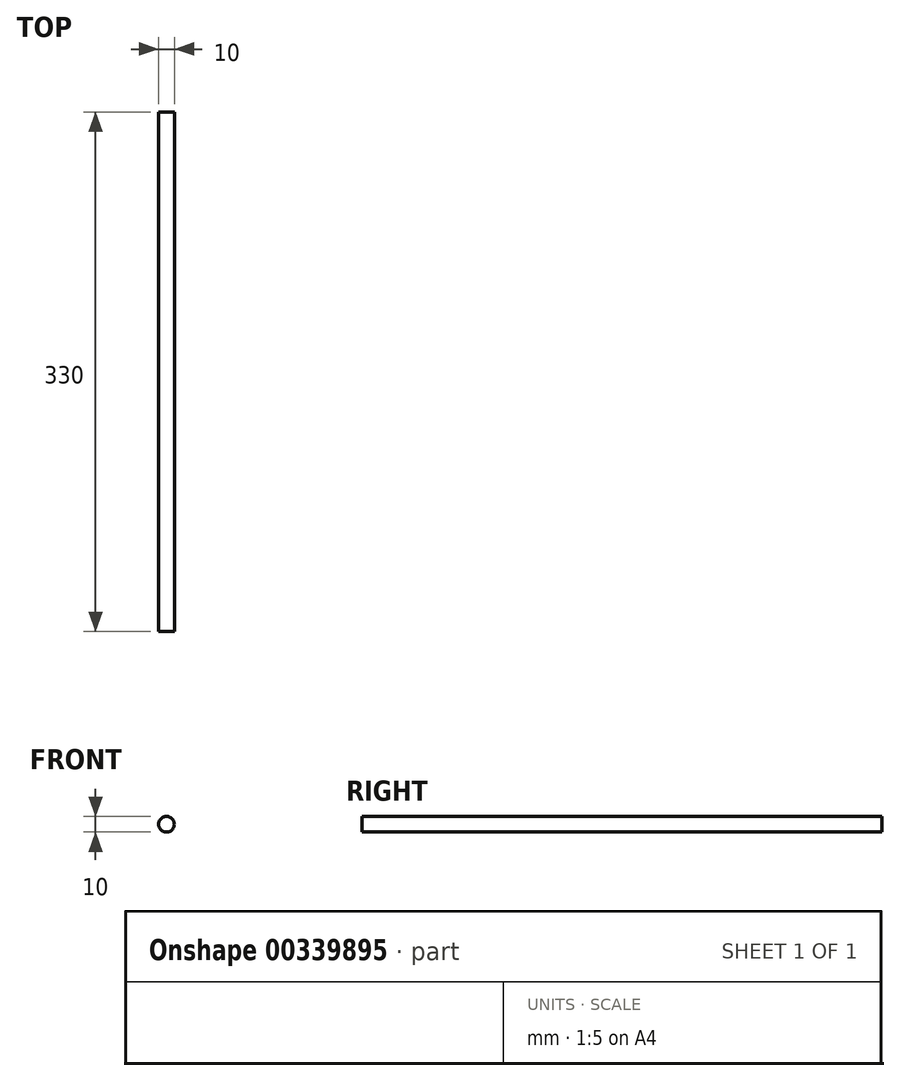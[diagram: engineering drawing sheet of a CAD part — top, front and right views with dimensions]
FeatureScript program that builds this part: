
annotation { "Feature Type Name" : "Feature", "Feature Type Description" : "" }
export const myFeature = defineFeature(function(context is Context, id is Id, definition is map)
    precondition{}
    {
        {
            var Q0;
            Q0=qCreatedBy(makeId("Front.planeOp"),FACE);
            var sketch = newSketch(context, id + "F0", { "sketchPlane" : qUnion([Q0])});
            skCircle(sketch, "E0", {"center": v(-36.9, 26.69) * mm, "radius": 5 * mm});
            skSolve(sketch);
        }
        {
            var Q0;
            Q0=makeQuery(id+"F0.imprint","IMPRINT",FACE,{"disambiguationData":[TD([[makeQuery(id+"F0.imprint","IMPRINT",EDGE,{"derivedFrom":sQuery(id+"F0.wireOp",EDGE,"E0")}),1.0]])]});
            extrude(context, id + "F1", {"entities" : qUnion([Q0]), "depth" : 330 * mm});
        }
    });
